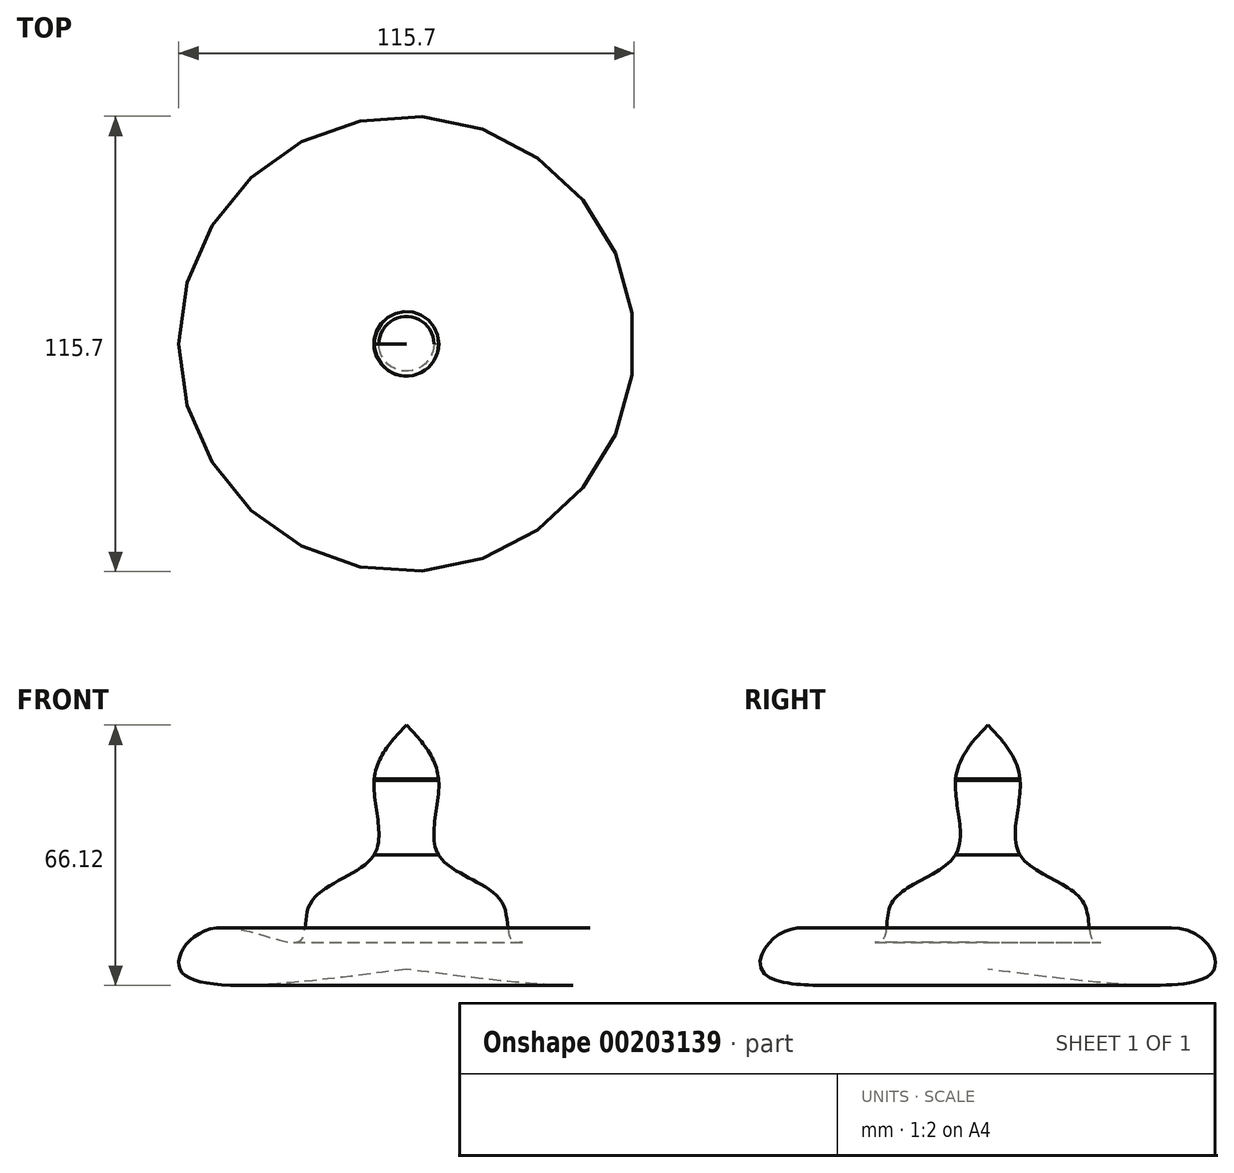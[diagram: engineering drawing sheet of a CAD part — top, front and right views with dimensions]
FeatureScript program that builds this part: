
annotation { "Feature Type Name" : "Feature", "Feature Type Description" : "" }
export const myFeature = defineFeature(function(context is Context, id is Id, definition is map)
    precondition{}
    {
        {
            var Q0;
            Q0=qCreatedBy(makeId("Front.planeOp"),FACE);
            var sketch = newSketch(context, id + "F0", { "sketchPlane" : qUnion([Q0])});
            skFitSpline(sketch, "E0", {"points": [v(0, 0) * mm, v(-57.52, 0) * mm, v(-49.05, 10.36) * mm, v(-27.15, 7.15) * mm, v(-24.23, 17.08) * mm, v(-8.18, 29.07) * mm, v(-8.17, 48.32) * mm, v(0, 62.04) * mm], "startDerivative": vector(-343.35, -44.9) * mm, "endDerivative": vector(85.03, 88.08) * mm});
            skLineSegment(sketch, "E1", {"start": v(0, 62.04) * mm, "end": v(0, 0) * mm});
            skArc(sketch, "E2", {"start": v(-37.58, 52.01) * mm, "mid": v(-23.61, 44.34) * mm, "end": v(-8.17, 48.32) * mm});
            skArc(sketch, "E3", {"start": v(-37.58, 52.01) * mm, "mid": v(-19.77, 50.97) * mm, "end": v(-3.54, 58.38) * mm});
            skArc(sketch, "E4", {"start": v(-43.46, 25.73) * mm, "mid": v(-25.44, 23.4) * mm, "end": v(-8.18, 29.07) * mm});
            skFitSpline(sketch, "E5", {"points": [v(-43.46, 25.73) * mm, v(-8.17, 48.32) * mm, v(-29.31, 64.21) * mm], "startDerivative": vector(94.27, 41.84) * mm, "endDerivative": vector(-72.34, 34.87) * mm});
            skLineSegment(sketch, "E6", {"start": v(0, 62.04) * mm, "end": v(-3.54, 58.38) * mm});
            skSolve(sketch);
        }
        {
            var Q0;
            Q0=makeQuery(id+"F0.imprint","IMPRINT",FACE,{"disambiguationData":[TD([[makeQuery(id+"F0.imprint","IMPRINT",EDGE,{"derivedFrom":sQuery(id+"F0.wireOp",EDGE,"E0")}),-1.0]])]});
            var Q1;
            Q1=sQuery(id+"F0.wireOp",EDGE,"E1");
            revolve(context, id + "F1", {"entities" : qUnion([Q0]), "axis" : qUnion([Q1]), "revolveType" : RevolveType.FULL});
        }
    });
